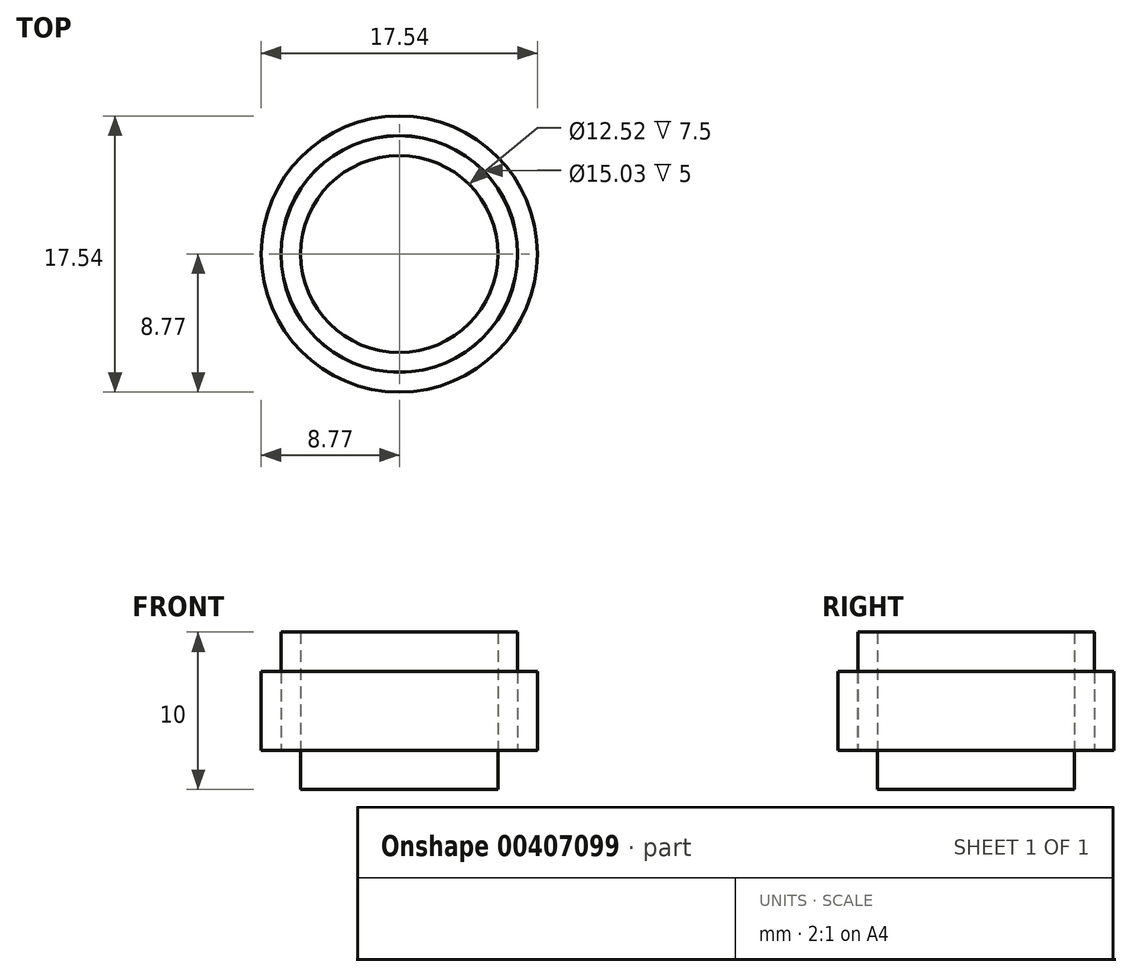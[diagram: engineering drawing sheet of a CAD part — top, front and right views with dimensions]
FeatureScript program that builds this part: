
annotation { "Feature Type Name" : "Feature", "Feature Type Description" : "" }
export const myFeature = defineFeature(function(context is Context, id is Id, definition is map)
    precondition{}
    {
        {
            var Q0;
            Q0=qCreatedBy(makeId("Top.planeOp"),FACE);
            var sketch = newSketch(context, id + "F0", { "sketchPlane" : qUnion([Q0])});
            skCircle(sketch, "E0", {"center": v(0, 0) * mm, "radius": 8.77 * mm});
            skCircle(sketch, "E1", {"center": v(0, 0) * mm, "radius": 7.5 * mm});
            skCircle(sketch, "E2", {"center": v(0, 0) * mm, "radius": 7.52 * mm});
            skCircle(sketch, "E3", {"center": v(0, 0) * mm, "radius": 6.26 * mm});
            skSolve(sketch);
        }
        {
            var Q0;
            Q0=makeQuery(id+"F0.imprint","IMPRINT",FACE,{"disambiguationData":[TD([[makeQuery(id+"F0.imprint","IMPRINT",EDGE,{"derivedFrom":sQuery(id+"F0.wireOp",EDGE,"E0")}),1.0]])]});
            extrude(context, id + "F1", {"entities" : qUnion([Q0]), "depth" : 5 * mm});
        }
        {
            var Q0;
            Q0=makeQuery(id+"F0.imprint","IMPRINT",FACE,{"disambiguationData":[TD([[makeQuery(id+"F0.imprint","IMPRINT",EDGE,{"derivedFrom":sQuery(id+"F0.wireOp",EDGE,"E1")}),1.0]])]});
            extrude(context, id + "F2", {"entities" : qUnion([Q0]), "depth" : 7.5 * mm});
        }
        {
            var Q0;
            Q0=makeQuery(id+"F0.imprint","IMPRINT",FACE,{"disambiguationData":[TD([[makeQuery(id+"F0.imprint","IMPRINT",EDGE,{"derivedFrom":sQuery(id+"F0.wireOp",EDGE,"E3")}),1.0]])]});
            extrude(context, id + "F3", {"entities" : qUnion([Q0]), "depth" : -2.5 * mm});
        }
    });
